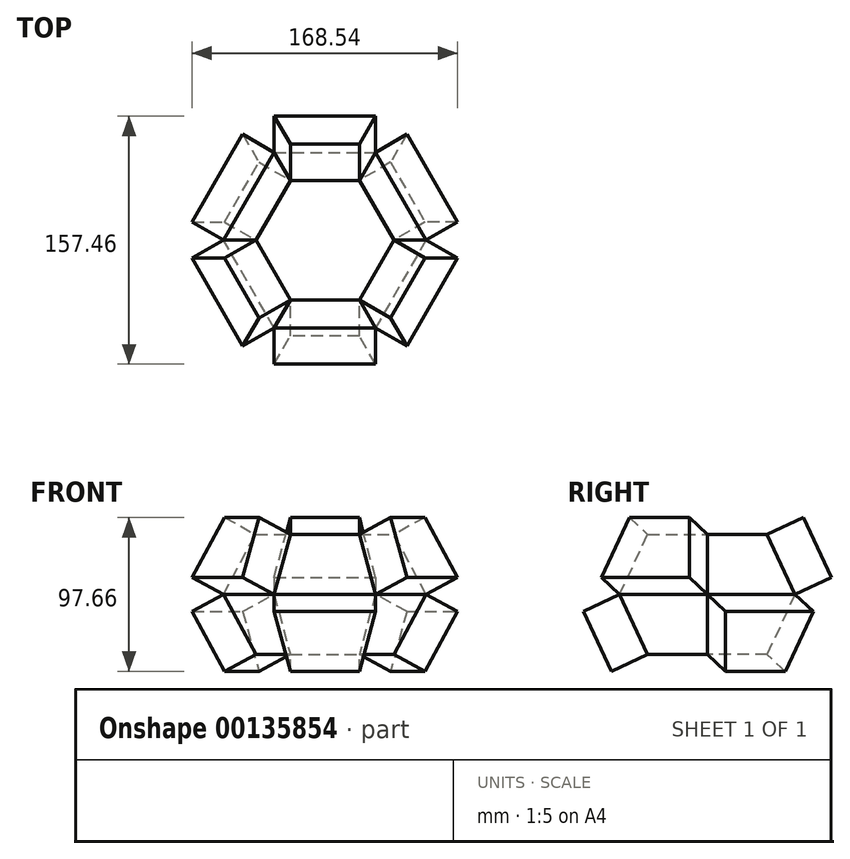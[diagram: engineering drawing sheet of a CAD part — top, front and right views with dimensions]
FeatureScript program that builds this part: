
annotation { "Feature Type Name" : "Feature", "Feature Type Description" : "" }
export const myFeature = defineFeature(function(context is Context, id is Id, definition is map)
    precondition{}
    {
        {
            var Q0;
            Q0=qCreatedBy(makeId("Top.planeOp"),FACE);
            var sketch = newSketch(context, id + "F0", { "sketchPlane" : qUnion([Q0])});
            skCircle(sketch, "E0.cCircle", {"center": v(0, 0) * mm, "radius": 37.95 * mm, "construction": true});
            skLineSegment(sketch, "E0.0", {"start": v(-21.9, 37.95) * mm, "end": v(21.9, 37.95) * mm});
            skLineSegment(sketch, "E0.1", {"start": v(21.9, 37.95) * mm, "end": v(43.82, 0) * mm});
            skLineSegment(sketch, "E0.2", {"start": v(43.82, 0) * mm, "end": v(21.9, -37.95) * mm});
            skLineSegment(sketch, "E0.3", {"start": v(21.9, -37.95) * mm, "end": v(-21.9, -37.95) * mm});
            skLineSegment(sketch, "E0.4", {"start": v(-21.9, -37.95) * mm, "end": v(-43.82, 0) * mm});
            skLineSegment(sketch, "E0.5", {"start": v(-43.82, 0) * mm, "end": v(-21.9, 37.95) * mm});
            skPoint(sketch, "E0.0.midPoint", {"position": v(0, 37.95) * mm});
            skSolve(sketch);
        }
        {
            var Q0;
            Q0 = qSketchRegion(id + "F0", true);
            extrude(context, id + "F1", {"entities" : qUnion([Q0]), "depth" : 38.1 * mm, "hasDraft" : true, "draftAngle" : 25 * degree});
        }
        {
            var Q0;
            Q0=makeQuery(id+"F1.opExtrude","SWEPT_BODY",BODY,{"disambiguationData":[OSD([sQuery(id+"F0.wireOp",EDGE,"E0.0"),sQuery(id+"F0.wireOp",EDGE,"E0.1"),sQuery(id+"F0.wireOp",EDGE,"E0.2"),sQuery(id+"F0.wireOp",EDGE,"E0.3"),sQuery(id+"F0.wireOp",EDGE,"E0.4"),sQuery(id+"F0.wireOp",EDGE,"E0.5")])]});
            var Q1;
            Q1=makeQuery(id+"F1.opExtrude","CAP_FACE",FACE,{"disambiguationData":[OSD([sQuery(id+"F0.wireOp",EDGE,"E0.0"),sQuery(id+"F0.wireOp",EDGE,"E0.1"),sQuery(id+"F0.wireOp",EDGE,"E0.2"),sQuery(id+"F0.wireOp",EDGE,"E0.3"),sQuery(id+"F0.wireOp",EDGE,"E0.4"),sQuery(id+"F0.wireOp",EDGE,"E0.5")])],"isStart":false});
            mirror(context, id + "F2", {"operationType" : NewBodyOperationType.ADD, "entities" : qUnion([Q0]), "mirrorPlane" : qUnion([Q1])});
        }
        {
            var Q0;
            Q0=makeQuery(id+"F1.opExtrude","SWEPT_FACE",FACE,{"disambiguationData":[OSD([sQuery(id+"F0.wireOp",EDGE,"E0.3")])]});
            extrude(context, id + "F3", {"entities" : qUnion([Q0]), "operationType" : NewBodyOperationType.ADD, "depth" : 25.4 * mm});
        }
        {
            var Q0;
            Q0=makeQuery(id+"F1.opExtrude","SWEPT_FACE",FACE,{"disambiguationData":[OSD([sQuery(id+"F0.wireOp",EDGE,"E0.5")])]});
            extrude(context, id + "F4", {"entities" : qUnion([Q0]), "operationType" : NewBodyOperationType.ADD, "depth" : 25.4 * mm});
        }
        {
            var Q0;
            Q0=makeQuery(id+"F1.opExtrude","SWEPT_FACE",FACE,{"disambiguationData":[OSD([sQuery(id+"F0.wireOp",EDGE,"E0.1")])]});
            extrude(context, id + "F5", {"entities" : qUnion([Q0]), "operationType" : NewBodyOperationType.ADD, "depth" : 25.4 * mm});
        }
        {
            var Q0;
            Q0=makeQuery(id+"F2.opPattern","COPY",FACE,{"derivedFrom":makeQuery(id+"F1.opExtrude","SWEPT_FACE",FACE,{"disambiguationData":[OSD([sQuery(id+"F0.wireOp",EDGE,"E0.2")])]}),"instanceName":"1"});
            extrude(context, id + "F6", {"entities" : qUnion([Q0]), "operationType" : NewBodyOperationType.ADD, "depth" : 25.4 * mm});
        }
        {
            var Q0;
            Q0=makeQuery(id+"F2.opPattern","COPY",FACE,{"derivedFrom":makeQuery(id+"F1.opExtrude","SWEPT_FACE",FACE,{"disambiguationData":[OSD([sQuery(id+"F0.wireOp",EDGE,"E0.4")])]}),"instanceName":"1"});
            extrude(context, id + "F7", {"entities" : qUnion([Q0]), "operationType" : NewBodyOperationType.ADD, "depth" : 25.4 * mm});
        }
        {
            var Q0;
            Q0=makeQuery(id+"F2.opPattern","COPY",FACE,{"derivedFrom":makeQuery(id+"F1.opExtrude","SWEPT_FACE",FACE,{"disambiguationData":[OSD([sQuery(id+"F0.wireOp",EDGE,"E0.0")])]}),"instanceName":"1"});
            extrude(context, id + "F8", {"entities" : qUnion([Q0]), "operationType" : NewBodyOperationType.ADD, "depth" : 25.4 * mm});
        }
    });
